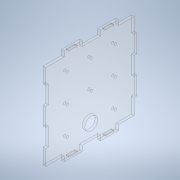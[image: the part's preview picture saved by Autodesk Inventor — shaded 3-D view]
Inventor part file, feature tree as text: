
AUTODESK INVENTOR PART (.ipt)
format: ipt  version: 2021 (Build 250183000, 183)  size: 196,096 bytes
history: native  units: mm
features: sketch x10, hole x9, extrude x1
ambient origin geometry x8: Origin, YZ Plane, XZ Plane, XY Plane, X Axis, Y Axis, Z Axis, Center Point
bodies: Solid1 (feature_tree)
feature tree (20):
  extrude  "Extrusion1"  Depth=3.0mm
  hole  "Hole2"  [1 undecoded]
  hole  "Hole3"  [1 undecoded]
  hole  "Hole4"  [1 undecoded]
  hole  "Hole5"  [1 undecoded]
  hole  "Hole6"  [1 undecoded]
  hole  "Hole7"  [1 undecoded]
  hole  "Hole8"  [1 undecoded]
  hole  "Hole9"  [1 undecoded]
  hole  "Hole10"  [1 undecoded]
  sketch  "Sketch1"  dims[d4=3.0mm d5=0.0mm d22=3.0mm]
  sketch  "Sketch3"  dims[d23=3.0mm d24=6.0mm d25=4.0mm d26=2.0mm d27=90.0deg d28=8.0mm d29=20.594885mm d30=3.0mm]
  sketch  "Sketch4"  dims[d31=3.0mm d32=6.0mm d33=4.0mm d34=2.0mm d35=90.0deg d36=8.0mm d37=20.594885mm d38=3.0mm]
  sketch  "Sketch5"  dims[d39=3.0mm d40=6.0mm d41=4.0mm d42=2.0mm d43=90.0deg d44=8.0mm d45=20.594885mm d46=3.0mm]
  sketch  "Sketch6"  dims[d47=15.0mm d48=6.0mm d49=4.0mm d50=2.0mm d51=90.0deg d52=8.0mm d53=20.594885mm d54=3.0mm]
  sketch  "Sketch7"  dims[d55=3.0mm d56=6.0mm d57=4.0mm d58=2.0mm d59=90.0deg d60=8.0mm d61=20.594885mm d62=3.0mm]
  sketch  "Sketch8"  dims[d63=3.0mm d64=6.0mm d65=4.0mm d66=2.0mm d67=90.0deg d68=8.0mm d69=20.594885mm d70=3.0mm]
  sketch  "Sketch9"  dims[d71=3.0mm d72=6.0mm d73=4.0mm d74=2.0mm d75=90.0deg d76=8.0mm d77=20.594885mm d78=3.0mm]
  sketch  "Sketch10"  dims[d79=3.0mm d80=6.0mm d81=4.0mm d82=2.0mm d83=90.0deg d84=8.0mm d85=20.594885mm d86=3.0mm]
  sketch  "Sketch11"  dims[d87=3.0mm d88=6.0mm d89=4.0mm d90=2.0mm d91=90.0deg d92=8.0mm d93=20.594885mm d94=1.0mm d95=10.0mm d96=1.0mm d97=1.0mm d98=10.0mm d99=10.0mm]
note: 9 required parameter values undecoded (feature->parameter linkage not recoverable at this tier; creation-order binding heuristic only, values carry confidence <= 0.55)
